# Revit family: SE - Weightbridge - P - UH
name_source: partatom
category: Specialty Equipment
units: mm (PartAtom-declared; Revit-internal decimal feet)

## family parameters
Always vertical = Yes
Cut with Voids When Loaded = No
Part Type = Normal
Room Calculation Point = No
Round Connector Dimension = Use Diameter
Shared = No
Work Plane-Based = No

## types (1)
- 7m x 3m
    Beam Width = 170 mm  [stored 0.557743 ft]
    Bridge Deck Thickness = 50 mm  [stored 0.164042 ft]
    Bridge Length = 7000 mm  [stored 22.9659 ft]
    Bridge Structure Thickness = 200 mm  [stored 0.656168 ft]
    Bridge Width = 3000 mm
    Concrete = Concrete
    Deck = Steel
    Default Elevation = 0 mm  [stored 0 ft]
    Foundation Depth = 2500 mm  [stored 8.2021 ft]
    Load Cell = Steel
    Load Cell Height = 200 mm  [stored 0.656168 ft]
    Load Cell Size = 250 mm  [stored 0.82021 ft]
    Max Support Spacing = 4000 mm  [stored 13.1234 ft]
    Ramp = Asphalt
    Ramp Length = 4500 mm
    Steel = Steel
    Support Count = 3
    Support Pile Diameter = 400 mm  [stored 1.31234 ft]
    Support Spacing Actual = 3250 mm  [stored 10.6627 ft]

note: [stored X ft] marks values corroborated as IEEE doubles in the binary element streams (Revit-internal decimal feet)

## geometry (parser evidence)
native form markers: Sweep x6
no freeform markers — native parametric forms only
